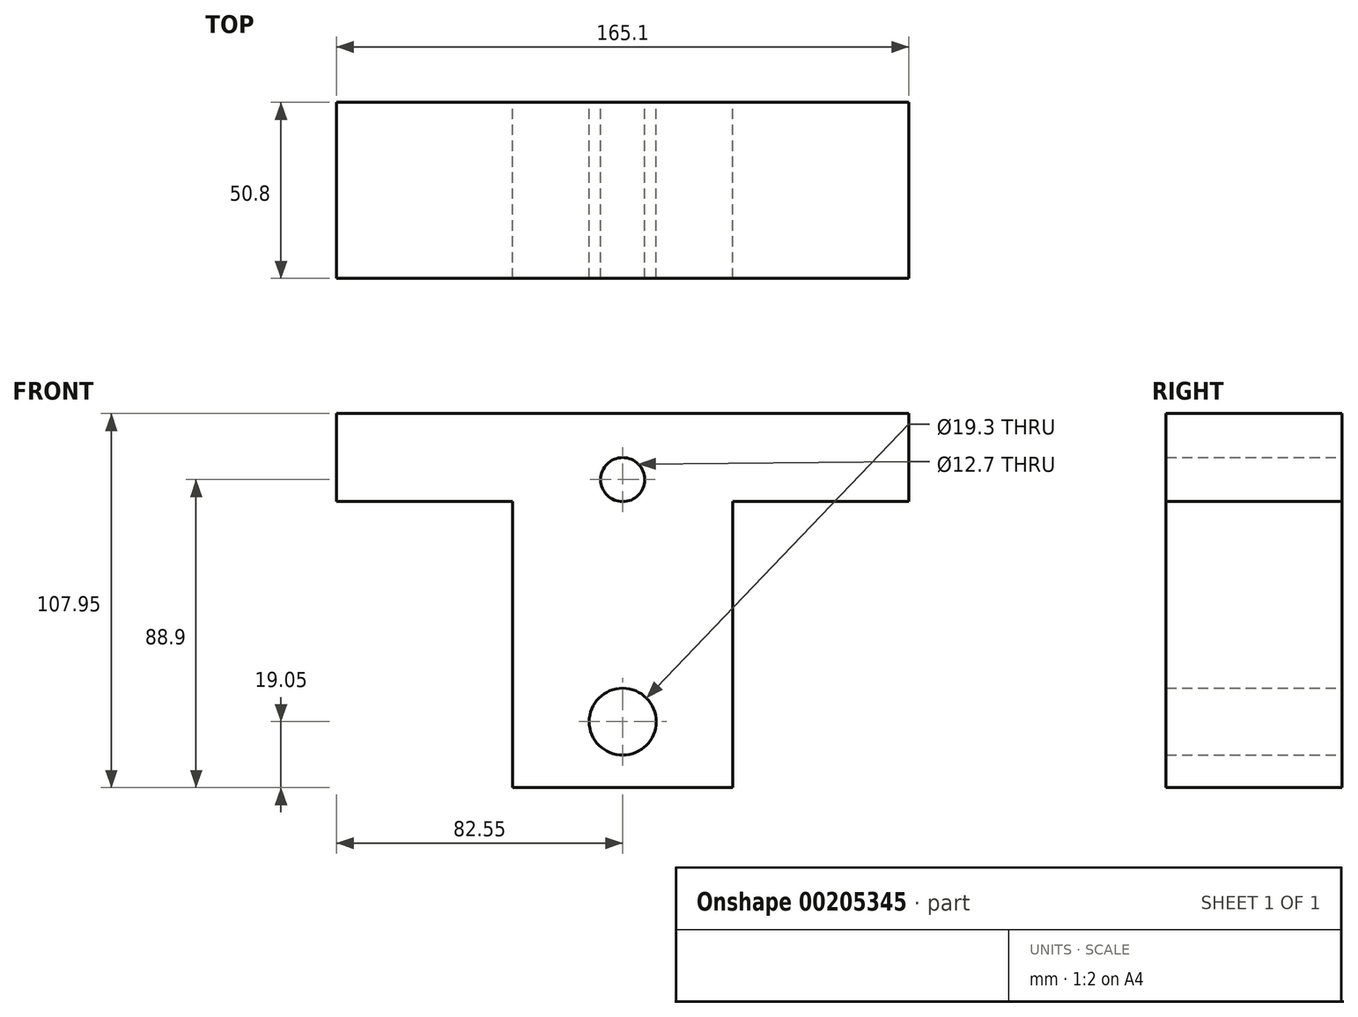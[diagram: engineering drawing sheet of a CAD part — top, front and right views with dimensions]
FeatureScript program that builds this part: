
annotation { "Feature Type Name" : "Feature", "Feature Type Description" : "" }
export const myFeature = defineFeature(function(context is Context, id is Id, definition is map)
    precondition{}
    {
        {
            var Q0;
            Q0=qCreatedBy(makeId("Front.planeOp"),FACE);
            var sketch = newSketch(context, id + "F0", { "sketchPlane" : qUnion([Q0])});
            skLineSegment(sketch, "E0", {"start": v(0, -19.05) * mm, "end": v(31.75, -19.05) * mm});
            skLineSegment(sketch, "E1", {"start": v(31.75, -19.05) * mm, "end": v(31.75, 63.5) * mm});
            skLineSegment(sketch, "E2", {"start": v(-31.75, 63.5) * mm, "end": v(-31.75, -19.05) * mm});
            skLineSegment(sketch, "E3", {"start": v(-31.75, -19.05) * mm, "end": v(0, -19.05) * mm});
            skLineSegment(sketch, "E4", {"start": v(31.75, 63.5) * mm, "end": v(82.55, 63.5) * mm});
            skLineSegment(sketch, "E5", {"start": v(82.55, 63.5) * mm, "end": v(82.55, 88.9) * mm});
            skLineSegment(sketch, "E6", {"start": v(82.55, 88.9) * mm, "end": v(-82.55, 88.9) * mm});
            skLineSegment(sketch, "E7", {"start": v(-82.55, 88.9) * mm, "end": v(-82.55, 63.5) * mm});
            skLineSegment(sketch, "E8", {"start": v(-82.55, 63.5) * mm, "end": v(-31.75, 63.5) * mm});
            skCircle(sketch, "E9", {"center": v(0, 0) * mm, "radius": 9.65 * mm});
            skLineSegment(sketch, "E10", {"start": v(0, 0) * mm, "end": v(0, 69.85) * mm});
            skCircle(sketch, "E11", {"center": v(0, 69.85) * mm, "radius": 6.35 * mm});
            skSolve(sketch);
        }
        {
            var Q0;
            Q0 = qSketchRegion(id + "F0", true);
            extrude(context, id + "F1", {"entities" : qUnion([Q0]), "depth" : 50.8 * mm});
        }
    });
